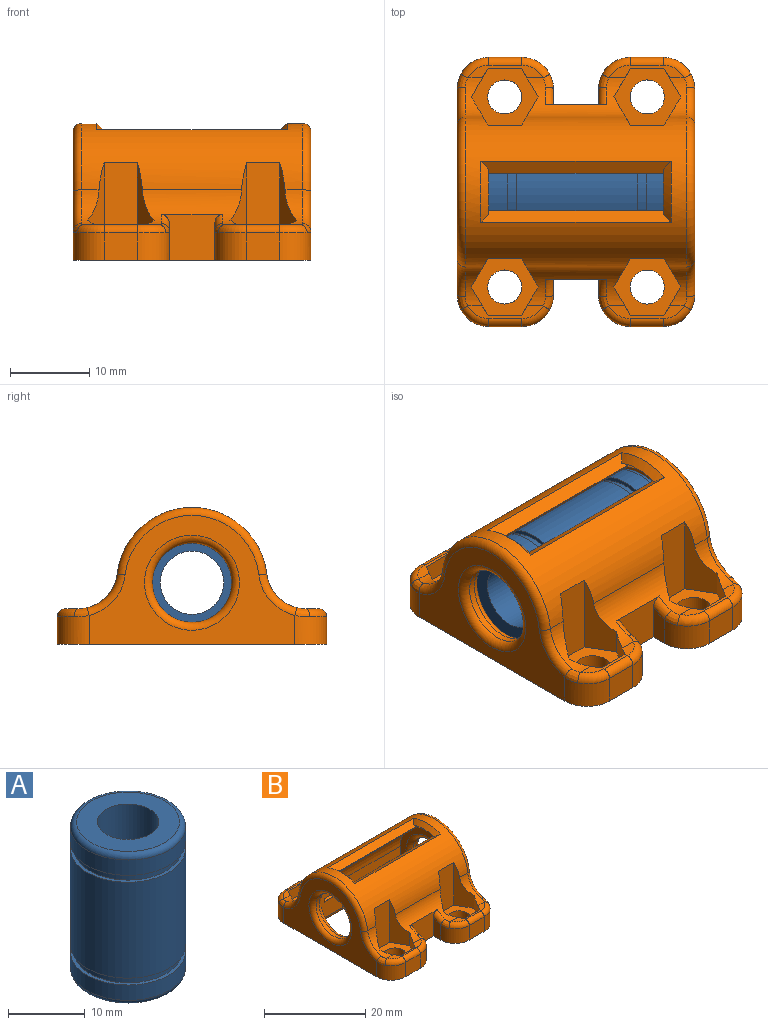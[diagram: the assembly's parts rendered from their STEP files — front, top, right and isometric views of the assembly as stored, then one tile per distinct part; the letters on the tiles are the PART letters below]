
ASSEMBLY  parts=2 mates=1
PART A: 14 faces, bbox 16.2x16.2x24 mm
  f0: cylinder r=7.5mm len=15mm, axis (0,0,-1), area 115.5mm2, adj f5,f12
  f1: cylinder r=4mm len=24mm, axis (0,0,-1), area 603.2mm2, adj f3,f4
  f2: cylinder r=7.5mm len=15mm, axis (0,0,-1), area 115.5mm2, adj f9,f13
  f3: plane 13.4x13.4mm, normal (0,0,1), area 90.8mm2, adj f1,f13
  f4: plane 13.4x13.4mm, normal (0,0,-1), area 90.8mm2, adj f1,f12
  f5: plane 15x15mm, normal (0,0,1), area 22.8mm2, adj f0,f6
  f6: cylinder r=7mm len=14mm, axis (0,0,1), area 48.4mm2, adj f5,f7
  f7: plane 15x15mm, normal (0,0,-1), area 22.8mm2, adj f6,f8
  f8: cylinder r=7.5mm len=15.3mm, axis (0,0,-1), area 721mm2, adj f7,f10
  f9: plane 15x15mm, normal (0,0,-1), area 22.8mm2, adj f2,f11
  f10: plane 15x15mm, normal (0,0,1), area 22.8mm2, adj f8,f11
  f11: cylinder r=7mm len=14mm, axis (0,0,1), area 48.4mm2, adj f9,f10
  f12: torus R=6.7mm, axis (0,0,1), area 56.9mm2, adj f0,f4
  f13: torus R=6.7mm, axis (0,0,1), area 56.9mm2, adj f2,f3
PART B: 133 faces, bbox 30.1x34.7x18.1 mm
  f0: plane 24.3x6.8mm, normal (0,1,0), area 160.4mm2, adj f14,f24,f26,f43,f125,f126,f127,f128
  f1: plane 24.3x6.8mm, normal (0,-1,0), area 160.4mm2, adj f14,f24,f26,f42,f117,f118,f119,f120
  f2: cylinder r=2.15mm len=4.3mm, axis (0,0,-1), area 27mm2, adj f21,f94
  f3: cylinder r=2.15mm len=4.3mm, axis (0,0,-1), area 27mm2, adj f21,f95
  f4: cylinder r=2.15mm len=4.3mm, axis (0,0,-1), area 27mm2, adj f21,f108
  f5: cylinder r=2.15mm len=4.3mm, axis (0,0,-1), area 27mm2, adj f21,f81
  f6: cylinder r=5mm len=4.97mm, axis (-1,0,0), area 11.7mm2, adj f20,f22,f55,f56,f103,f104
  f7: cylinder r=5mm len=4.97mm, axis (-1,0,0), area 11.7mm2, adj f11,f22,f70,f71,f97,f98
  f8: cylinder r=5mm len=4.97mm, axis (-1,0,0), area 11.7mm2, adj f16,f22,f67,f68,f89,f90
  f9: cylinder r=5mm len=4.97mm, axis (-1,0,0), area 11.7mm2, adj f10,f22,f52,f53,f83,f84
  f10: plane 9.46x1.6mm, normal (0,0,1), area 6.5mm2, adj f9,f46,f49,f50,f51,f84,f85,f86
  f11: plane 9.46x1.6mm, normal (0,0,1), area 6.5mm2, adj f7,f45,f72,f73,f74,f98,f99,f100
  f12: plane 4.15x3.5mm, normal (0,-1,0), area 14.5mm2, adj f21,f33,f38,f73
  f13: plane 4.15x3.5mm, normal (0,1,0), area 14.5mm2, adj f21,f36,f39,f65
  f14: cylinder r=7.6mm len=24.3mm, axis (-1,0,0), area 441.4mm2, adj f0,f1,f24,f26,f109,f111,f114,f116
  f15: plane 26x16.3mm, normal (-1,0,0), area 178.8mm2, adj f21,f37,f40,f53,f54,f55,f79
  f16: plane 9.46x1.6mm, normal (0,0,1), area 6.5mm2, adj f8,f46,f64,f65,f66,f90,f91,f92
  f17: plane 4.15x3.5mm, normal (0,-1,0), area 14.5mm2, adj f21,f34,f37,f58
  f18: plane 26x16.3mm, normal (1,0,0), area 178.8mm2, adj f21,f38,f39,f68,f69,f70,f78
  f19: plane 4.15x3.5mm, normal (0,1,0), area 14.5mm2, adj f21,f35,f40,f50
  f20: plane 9.46x1.6mm, normal (0,0,1), area 6.5mm2, adj f6,f45,f57,f58,f59,f104,f105,f106
  f21: plane 34x30mm, normal (0,0,-1), area 413.7mm2, adj f2,f3,f4,f5,f12,f13,f15,f17
  f22: cylinder r=9.5mm len=28mm, axis (-1,0,0), area 511.8mm2, adj f6,f7,f8,f9,f45,f46,f54,f69
  f23: cylinder r=5mm len=10mm, axis (-1,0,0), area 26.7mm2, adj f79,f80
  f24: plane 15.2x14.4mm, normal (1,0,0), area 81mm2, adj f0,f1,f14,f41,f80
  f25: cylinder r=5mm len=10mm, axis (1,0,0), area 26.7mm2, adj f77,f78
  f26: plane 15.2x14.4mm, normal (-1,0,0), area 81mm2, adj f0,f1,f14,f44,f77
  f27: plane 4.56x2mm, normal (-1,0,0), area 8.1mm2, adj f21,f28,f33,f76
  f28: plane 7.7x5.83mm, normal (0,-1,0), area 33.8mm2, adj f21,f27,f29,f45,f61,f76
  f29: plane 4.56x2mm, normal (1,0,0), area 8.1mm2, adj f21,f28,f34,f61
  f30: plane 4.56x2mm, normal (1,0,0), area 8.1mm2, adj f21,f31,f35,f47
  f31: plane 7.7x5.83mm, normal (0,1,0), area 33.8mm2, adj f21,f30,f32,f46,f47,f62
  f32: plane 4.56x2mm, normal (-1,0,0), area 8.1mm2, adj f21,f31,f36,f62
  f33: cylinder r=4mm len=4mm, axis (0,0,1), area 22.1mm2, adj f12,f21,f27,f74,f75
  f34: cylinder r=4mm len=4mm, axis (0,0,-1), area 22.1mm2, adj f17,f21,f29,f59,f60
  f35: cylinder r=4mm len=4mm, axis (0,0,-1), area 22.1mm2, adj f19,f21,f30,f48,f49
  f36: cylinder r=4mm len=4mm, axis (0,0,1), area 22.1mm2, adj f13,f21,f32,f63,f64
  f37: cylinder r=4mm len=4mm, axis (0,0,-1), area 22.1mm2, adj f15,f17,f21,f56,f57
  f38: cylinder r=4mm len=4mm, axis (0,0,1), area 22.1mm2, adj f12,f18,f21,f71,f72
  f39: cylinder r=4mm len=4mm, axis (0,0,-1), area 22.1mm2, adj f13,f18,f21,f66,f67
  f40: cylinder r=4mm len=4mm, axis (0,0,1), area 22.1mm2, adj f15,f19,f21,f51,f52
  f41: cylinder r=1mm len=17.2mm, axis (0,-1,0), area 25mm2, adj f21,f24,f42,f43
  f42: cylinder r=1mm len=26.3mm, axis (-1,0,0), area 39.3mm2, adj f1,f21,f41,f44
  f43: cylinder r=1mm len=26.3mm, axis (1,0,0), area 39.3mm2, adj f0,f21,f41,f44
  f44: cylinder r=1mm len=17.2mm, axis (0,-1,0), area 25mm2, adj f21,f26,f42,f43
  f45: cylinder r=5mm len=12.53mm, axis (-1,0,0), area 52.7mm2, adj f11,f20,f22,f28,f60,f61,f75,f76
  f46: cylinder r=5mm len=12.53mm, axis (-1,0,0), area 52.7mm2, adj f10,f16,f22,f31,f47,f48,f62,f63
  f47: torus R=6mm, axis (-1,0,0), area 3.8mm2, adj f30,f31,f46,f48
  f48: bspline ~3.49x1.73mm, area 2.5mm2, adj f35,f46,f47,f49
  f49: torus R=3mm, axis (0,0,1), area 6.2mm2, adj f10,f35,f48,f50
  f50: cylinder r=1mm len=4.15mm, axis (1,0,0), area 6.5mm2, adj f10,f19,f49,f51
  f51: torus R=3mm, axis (0,0,1), area 6.2mm2, adj f10,f40,f50,f52
  f52: bspline ~3.49x1.73mm, area 2.5mm2, adj f9,f40,f51,f53
  f53: torus R=6mm, axis (1,0,0), area 10.3mm2, adj f9,f15,f52,f54
  f54: torus R=8.5mm, axis (1,0,0), area 41.7mm2, adj f15,f22,f53,f55
  f55: torus R=6mm, axis (1,0,0), area 10.3mm2, adj f6,f15,f54,f56
  f56: bspline ~3.49x1.73mm, area 2.5mm2, adj f6,f37,f55,f57
  f57: torus R=3mm, axis (0,0,1), area 6.2mm2, adj f20,f37,f56,f58
  f58: cylinder r=1mm len=4.15mm, axis (-1,0,0), area 6.5mm2, adj f17,f20,f57,f59
  f59: torus R=3mm, axis (0,0,1), area 6.2mm2, adj f20,f34,f58,f60
  f60: bspline ~3.49x1.73mm, area 2.5mm2, adj f34,f45,f59,f61
  f61: torus R=6mm, axis (1,0,0), area 3.8mm2, adj f28,f29,f45,f60
  f62: torus R=6mm, axis (-1,0,0), area 3.8mm2, adj f31,f32,f46,f63
  f63: bspline ~3.49x1.73mm, area 2.5mm2, adj f36,f46,f62,f64
  f64: torus R=3mm, axis (0,0,1), area 6.2mm2, adj f16,f36,f63,f65
  f65: cylinder r=1mm len=4.15mm, axis (1,0,0), area 6.5mm2, adj f13,f16,f64,f66
  f66: torus R=3mm, axis (0,0,1), area 6.2mm2, adj f16,f39,f65,f67
  f67: bspline ~3.49x1.73mm, area 2.5mm2, adj f8,f39,f66,f68
  f68: torus R=6mm, axis (1,0,0), area 10.3mm2, adj f8,f18,f67,f69
  f69: torus R=8.5mm, axis (1,0,0), area 41.7mm2, adj f18,f22,f68,f70
  f70: torus R=6mm, axis (1,0,0), area 10.3mm2, adj f7,f18,f69,f71
  f71: bspline ~3.49x1.73mm, area 2.5mm2, adj f7,f38,f70,f72
  f72: torus R=3mm, axis (0,0,1), area 6.2mm2, adj f11,f38,f71,f73
  f73: cylinder r=1mm len=4.15mm, axis (-1,0,0), area 6.5mm2, adj f11,f12,f72,f74
  f74: torus R=3mm, axis (0,0,1), area 6.2mm2, adj f11,f33,f73,f75
  f75: bspline ~3.49x1.73mm, area 2.5mm2, adj f33,f45,f74,f76
  f76: torus R=6mm, axis (1,0,0), area 3.8mm2, adj f27,f28,f45,f75
  f77: torus R=6mm, axis (1,0,0), area 52.9mm2, adj f25,f26
  f78: torus R=6mm, axis (1,0,0), area 52.9mm2, adj f18,f25
  f79: torus R=6mm, axis (1,0,0), area 52.9mm2, adj f15,f23
  f80: torus R=6mm, axis (-1,0,0), area 52.9mm2, adj f23,f24
  f81: plane 8.43x7.3mm, normal (0,0,1), area 31.6mm2, adj f5,f82,f83,f84,f85,f86,f87
  f82: plane 10.33x4.21mm, normal (0,1,0), area 43.5mm2, adj f22,f81,f83,f87
  f83: plane 10.33x3.65mm, normal (0.87,0.5,0), area 24.1mm2, adj f9,f22,f81,f82,f84
  f84: plane 3.7x3.16mm, normal (0.87,-0.5,0), area 11.1mm2, adj f9,f10,f81,f83,f85
  f85: plane 4.21x2.5mm, normal (0,-1,0), area 10.5mm2, adj f10,f81,f84,f86
  f86: plane 3.7x3.16mm, normal (-0.87,-0.5,0), area 11.1mm2, adj f10,f46,f81,f85,f87
  f87: plane 10.33x3.65mm, normal (-0.87,0.5,0), area 24.1mm2, adj f22,f46,f81,f82,f86
  f88: plane 10.33x4.21mm, normal (0,1,0), area 43.5mm2, adj f22,f89,f93,f94
  f89: plane 10.33x3.65mm, normal (-0.87,0.5,0), area 24.1mm2, adj f8,f22,f88,f90,f94
  f90: plane 3.7x3.16mm, normal (-0.87,-0.5,0), area 11.1mm2, adj f8,f16,f89,f91,f94
  f91: plane 4.21x2.5mm, normal (0,-1,0), area 10.5mm2, adj f16,f90,f92,f94
  f92: plane 3.7x3.16mm, normal (0.87,-0.5,0), area 11.1mm2, adj f16,f46,f91,f93,f94
  f93: plane 10.33x3.65mm, normal (0.87,0.5,0), area 24.1mm2, adj f22,f46,f88,f92,f94
  f94: plane 8.43x7.3mm, normal (0,0,1), area 31.6mm2, adj f2,f88,f89,f90,f91,f92,f93
  f95: plane 8.43x7.3mm, normal (0,0,1), area 31.6mm2, adj f3,f96,f97,f98,f99,f100,f101
  f96: plane 10.33x4.21mm, normal (0,-1,0), area 43.5mm2, adj f22,f95,f97,f101
  f97: plane 10.33x3.65mm, normal (-0.87,-0.5,0), area 24.1mm2, adj f7,f22,f95,f96,f98
  f98: plane 3.7x3.16mm, normal (-0.87,0.5,0), area 11.1mm2, adj f7,f11,f95,f97,f99
  f99: plane 4.21x2.5mm, normal (0,1,0), area 10.5mm2, adj f11,f95,f98,f100
  f100: plane 3.7x3.16mm, normal (0.87,0.5,0), area 11.1mm2, adj f11,f45,f95,f99,f101
  f101: plane 10.33x3.65mm, normal (0.87,-0.5,0), area 24.1mm2, adj f22,f45,f95,f96,f100
  f102: plane 10.33x4.21mm, normal (0,-1,0), area 43.5mm2, adj f22,f103,f107,f108
  f103: plane 10.33x3.65mm, normal (0.87,-0.5,0), area 24.1mm2, adj f6,f22,f102,f104,f108
  f104: plane 3.7x3.16mm, normal (0.87,0.5,0), area 11.1mm2, adj f6,f20,f103,f105,f108
  f105: plane 4.21x2.5mm, normal (0,1,0), area 10.5mm2, adj f20,f104,f106,f108
  f106: plane 3.7x3.16mm, normal (-0.87,0.5,0), area 11.1mm2, adj f20,f45,f105,f107,f108
  f107: plane 10.33x3.65mm, normal (-0.87,-0.5,0), area 24.1mm2, adj f22,f45,f102,f106,f108
  f108: plane 8.43x7.3mm, normal (0,0,1), area 31.6mm2, adj f4,f102,f103,f104,f105,f106,f107
  f109: plane 24.03x0.7mm, normal (0,-0.83,-0.56), area 19.2mm2, adj f14,f110,f114,f116
  f110: plane 24.04x1.51mm, normal (0,-0.55,0.84), area 40.2mm2, adj f22,f109,f113,f114,f115,f116
  f111: plane 24.03x0.7mm, normal (0,0.83,-0.56), area 19.2mm2, adj f14,f112,f114,f116
  f112: plane 24.04x1.51mm, normal (0,0.55,0.84), area 40.2mm2, adj f22,f111,f113,f114,f115,f116
  f113: cone r=8.5mm half-angle=45deg, axis (-1,0,0), area 9.2mm2, adj f22,f110,f112,f114
  f114: cone r=7.6mm half-angle=45deg, axis (1,0,0), area 7.1mm2, adj f14,f109,f110,f111,f112,f113
  f115: cone r=9.5mm half-angle=45deg, axis (1,0,0), area 9.2mm2, adj f22,f110,f112,f116
  f116: cone r=8.6mm half-angle=45deg, axis (-1,0,0), area 7.1mm2, adj f14,f109,f110,f111,f112,f115
  f117: plane 0.8x0.4mm, normal (-1,0,0), area 0.2mm2, adj f1,f119,f120
  f118: plane 0.8x0.4mm, normal (1,0,0), area 0.2mm2, adj f1,f119,f120
  f119: plane 3x0.4mm, normal (0,-0.71,0.71), area 1.7mm2, adj f1,f117,f118,f120
  f120: plane 3x0.4mm, normal (0,-0.71,-0.71), area 1.7mm2, adj f1,f117,f118,f119
  f121: plane 0.8x0.4mm, normal (1,0,0), area 0.2mm2, adj f1,f123,f124
  f122: plane 0.8x0.4mm, normal (-1,0,0), area 0.2mm2, adj f1,f123,f124
  f123: plane 3x0.4mm, normal (0,-0.71,0.71), area 1.7mm2, adj f1,f121,f122,f124
  f124: plane 3x0.4mm, normal (0,-0.71,-0.71), area 1.7mm2, adj f1,f121,f122,f123
  f125: plane 0.8x0.4mm, normal (-1,0,0), area 0.2mm2, adj f0,f127,f128
  f126: plane 0.8x0.4mm, normal (1,0,0), area 0.2mm2, adj f0,f127,f128
  f127: plane 3x0.4mm, normal (0,0.71,0.71), area 1.7mm2, adj f0,f125,f126,f128
  f128: plane 3x0.4mm, normal (0,0.71,-0.71), area 1.7mm2, adj f0,f125,f126,f127
  f129: plane 0.8x0.4mm, normal (1,0,0), area 0.2mm2, adj f0,f131,f132
  f130: plane 0.8x0.4mm, normal (-1,0,0), area 0.2mm2, adj f0,f131,f132
  f131: plane 3x0.4mm, normal (0,0.71,0.71), area 1.7mm2, adj f0,f129,f130,f132
  f132: plane 3x0.4mm, normal (0,0.71,-0.71), area 1.7mm2, adj f0,f129,f130,f131
PLACE A rot(axis=(0,1,0),90deg) t=(-11.85,0,7.8)mm
PLACE B at identity
MATE fastened A.f0 <-> B.f25  axis (1,0,0) through (12.15,0,7.8)mm
